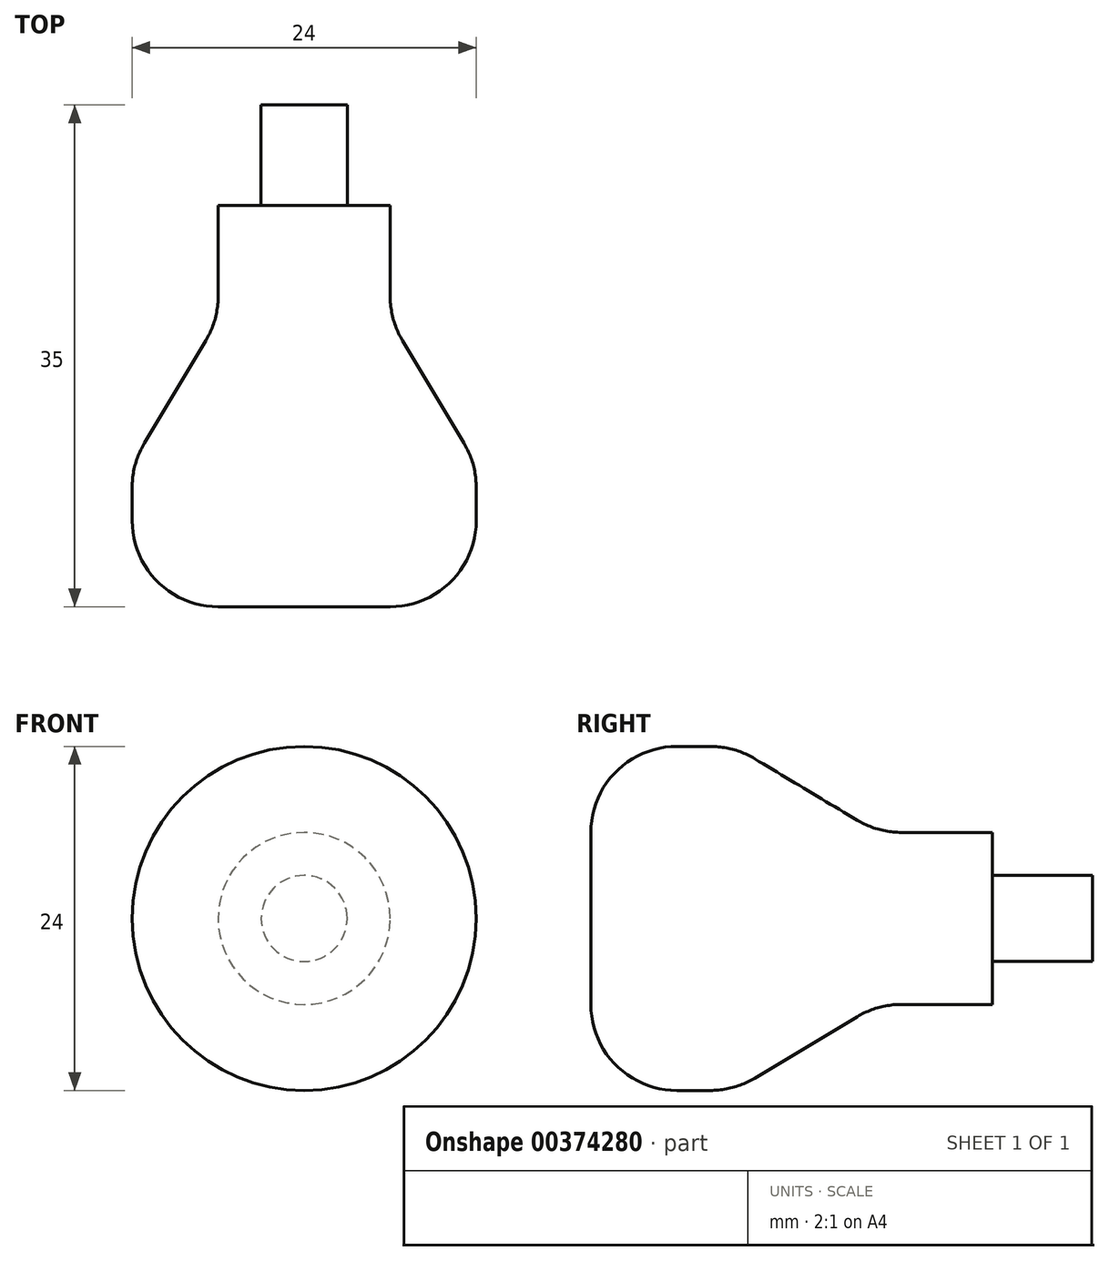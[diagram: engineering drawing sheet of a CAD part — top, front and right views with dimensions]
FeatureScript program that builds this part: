
annotation { "Feature Type Name" : "Feature", "Feature Type Description" : "" }
export const myFeature = defineFeature(function(context is Context, id is Id, definition is map)
    precondition{}
    {
        {
            var Q0;
            Q0=qCreatedBy(makeId("Right.planeOp"),FACE);
            var sketch = newSketch(context, id + "F0", { "sketchPlane" : qUnion([Q0])});
            skLineSegment(sketch, "E0", {"start": v(11.14, 0) * mm, "end": v(-23.86, 0) * mm});
            skLineSegment(sketch, "E1", {"start": v(-23.86, 0) * mm, "end": v(-23.86, -6) * mm});
            skLineSegment(sketch, "E2", {"start": v(-17.86, -12) * mm, "end": v(-15.52, -12) * mm});
            skLineSegment(sketch, "E3", {"start": v(-12.44, -11.14) * mm, "end": v(-5.29, -6.86) * mm});
            skLineSegment(sketch, "E4", {"start": v(-2.2, -6) * mm, "end": v(4.14, -6) * mm});
            skLineSegment(sketch, "E5", {"start": v(4.14, -6) * mm, "end": v(4.14, -3) * mm});
            skLineSegment(sketch, "E6", {"start": v(4.14, -3) * mm, "end": v(11.14, -3) * mm});
            skLineSegment(sketch, "E7", {"start": v(11.14, -3) * mm, "end": v(11.14, 0) * mm});
            skPoint(sketch, "E8.visualSharp", {"position": v(-23.86, -12) * mm});
            skArc(sketch, "E8.filletArc", {"start": v(-23.86, -6) * mm, "mid": v(-22.1, -10.24) * mm, "end": v(-17.86, -12) * mm});
            skPoint(sketch, "E9.visualSharp", {"position": v(-13.86, -12) * mm});
            skArc(sketch, "E9.filletArc", {"start": v(-15.52, -12) * mm, "mid": v(-13.92, -11.78) * mm, "end": v(-12.44, -11.14) * mm});
            skPoint(sketch, "E10.visualSharp", {"position": v(-3.86, -6) * mm});
            skArc(sketch, "E10.filletArc", {"start": v(-2.2, -6) * mm, "mid": v(-3.8, -6.22) * mm, "end": v(-5.29, -6.86) * mm});
            skSolve(sketch);
        }
        {
            var Q0;
            Q0=makeQuery(id+"F0.imprint","IMPRINT",FACE,{"disambiguationData":[TD([[makeQuery(id+"F0.imprint","IMPRINT",EDGE,{"derivedFrom":sQuery(id+"F0.wireOp",EDGE,"E0")}),1.0]])]});
            var Q1;
            Q1=sQuery(id+"F0.wireOp",EDGE,"E0");
            revolve(context, id + "F1", {"entities" : qUnion([Q0]), "axis" : qUnion([Q1]), "revolveType" : RevolveType.FULL});
        }
    });
